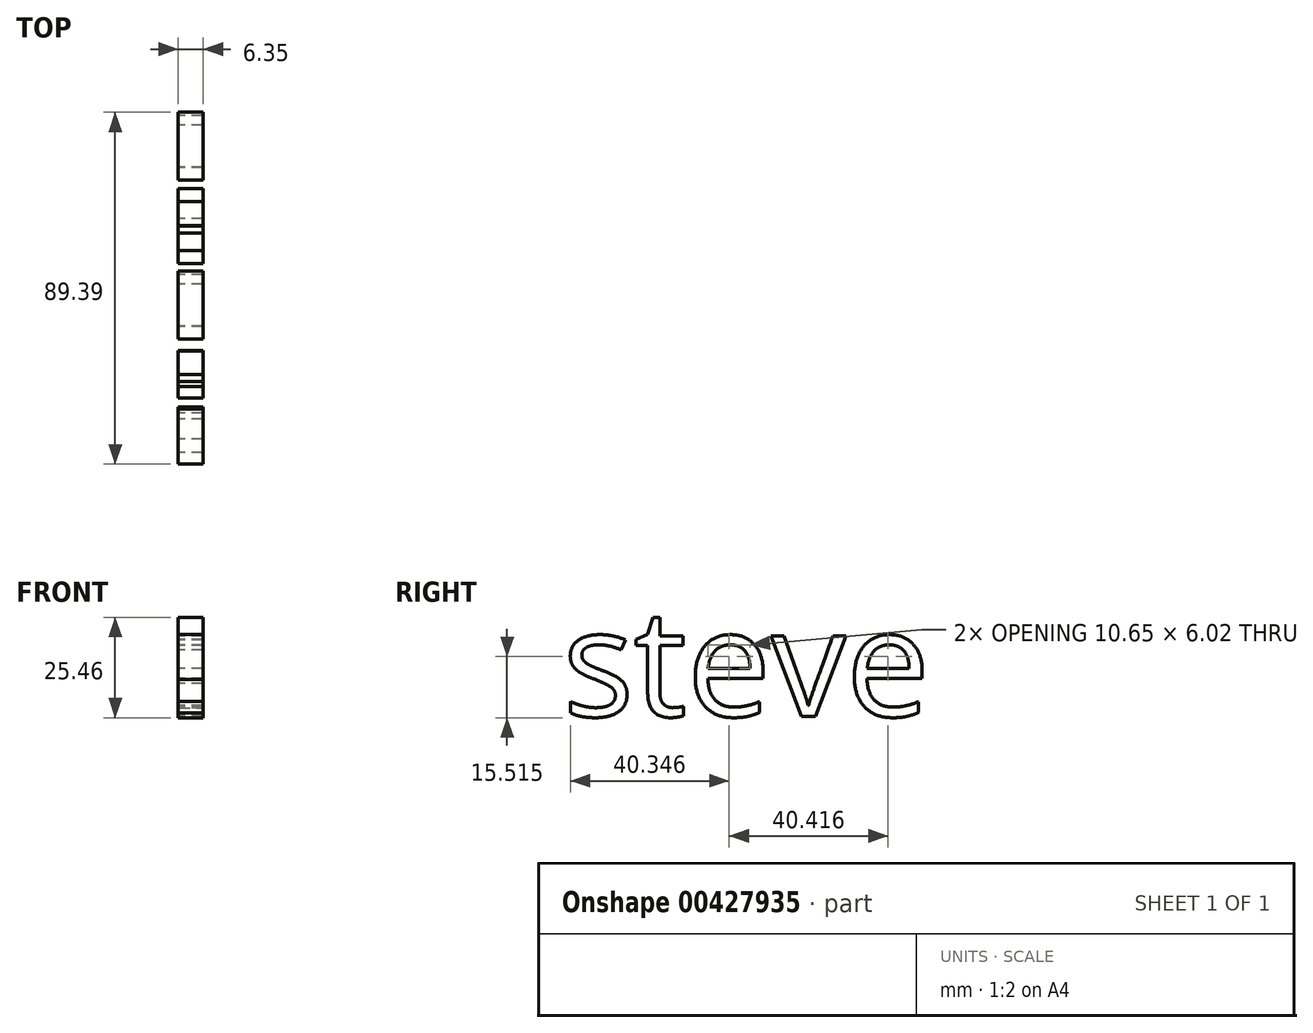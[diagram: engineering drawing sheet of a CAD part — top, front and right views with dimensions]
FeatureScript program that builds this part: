
annotation { "Feature Type Name" : "Feature", "Feature Type Description" : "" }
export const myFeature = defineFeature(function(context is Context, id is Id, definition is map)
    precondition{}
    {
        {
            var Q0;
            Q0=qCreatedBy(makeId("Right.planeOp"),FACE);
            var sketch = newSketch(context, id + "F0", { "sketchPlane" : qUnion([Q0])});
            skText(sketch, "E0", { "text": "steve\n", "fontName": "OpenSans-Regular.ttf"});
            const initialGuessF0  = {"E0": [-0.05537, 0.0212, 1, 0, 0.0274]};
            skSetInitialGuess(sketch, initialGuessF0);
            skSolve(sketch);
        }
        {
            var Q0;
            Q0 = qSketchRegion(id + "F0", true);
            extrude(context, id + "F1", {"entities" : qUnion([Q0]), "depth" : 6.35 * mm});
        }
    });
